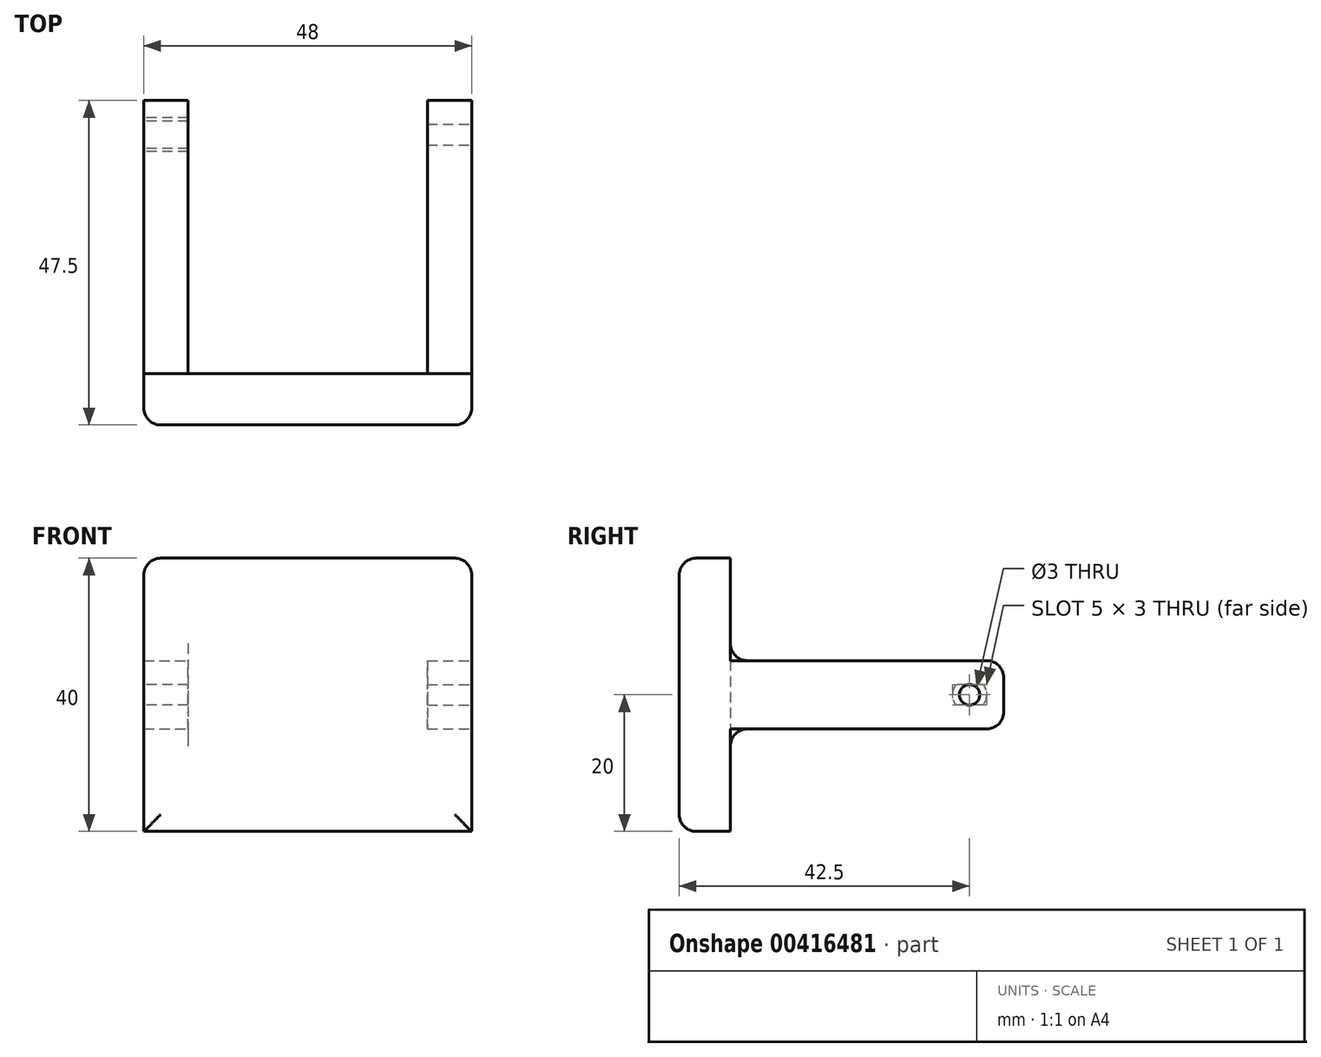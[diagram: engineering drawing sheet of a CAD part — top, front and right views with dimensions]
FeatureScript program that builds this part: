
annotation { "Feature Type Name" : "Feature", "Feature Type Description" : "" }
export const myFeature = defineFeature(function(context is Context, id is Id, definition is map)
    precondition{}
    {
        {
            var Q0;
            Q0=qCreatedBy(makeId("Top.planeOp"),FACE);
            var sketch = newSketch(context, id + "F0", { "sketchPlane" : qUnion([Q0])});
            skLineSegment(sketch, "E0.bottom", {"start": v(-24, 40) * mm, "end": v(24, 40) * mm});
            skLineSegment(sketch, "E0.top", {"start": v(-24, -7.5) * mm, "end": v(24, -7.5) * mm});
            skLineSegment(sketch, "E0.left", {"start": v(-24, 40) * mm, "end": v(-24, -7.5) * mm});
            skLineSegment(sketch, "E0.right", {"start": v(24, 40) * mm, "end": v(24, -7.5) * mm});
            skLineSegment(sketch, "E1.bottom", {"start": v(-17.5, 40) * mm, "end": v(17.5, 40) * mm});
            skLineSegment(sketch, "E1.top", {"start": v(-17.5, 0) * mm, "end": v(17.5, 0) * mm});
            skLineSegment(sketch, "E1.left", {"start": v(-17.5, 40) * mm, "end": v(-17.5, 0) * mm});
            skLineSegment(sketch, "E1.right", {"start": v(17.5, 40) * mm, "end": v(17.5, 0) * mm});
            skPoint(sketch, "E2", {"position": v(0, 40) * mm});
            skPoint(sketch, "E3", {"position": v(0, 0) * mm});
            skLineSegment(sketch, "E4.top", {"start": v(-24, 0) * mm, "end": v(24, 0) * mm});
            skLineSegment(sketch, "E4.left", {"start": v(-24, -7.5) * mm, "end": v(-24, 0) * mm});
            skLineSegment(sketch, "E4.right", {"start": v(24, -7.5) * mm, "end": v(24, 0) * mm});
            skSolve(sketch);
        }
        {
            var Q0;
            {var subQ0=sQuery(id+"F0.wireOp",EDGE,"fILYmVWM-iYGu-gwed-nY9A-4RlSeJw38Jqi.bottom");var subQ1=sQuery(id+"F0.wireOp",EDGE,"E0.left");var subQ2=makeQuery(id+"F0.imprint","INTERSECT",VERTEX,{"derivedFrom":[subQ1,subQ0]});Q0=makeQuery(id+"F0.imprint","IMPRINT",FACE,{"disambiguationData":[TD([[makeQuery(id+"F0.imprint","IMPRINT",EDGE,{"disambiguationData":[TD([[subQ2,1.0]])],"derivedFrom":subQ1}),1.0]])]});}
            var Q1;
            {var subQ3=sQuery(id+"F0.wireOp",EDGE,"E1.left");Q1=makeQuery(id+"F0.imprint","IMPRINT",FACE,{"disambiguationData":[TD([[makeQuery(id+"F0.imprint","IMPRINT",EDGE,{"derivedFrom":subQ3}),-1.0]])]});}
            var Q2;
            {var subQ5=sQuery(id+"F0.wireOp",EDGE,"fILYmVWM-iYGu-gwed-nY9A-4RlSeJw38Jqi.left");Q2=makeQuery(id+"F0.imprint","IMPRINT",FACE,{"disambiguationData":[TD([[makeQuery(id+"F0.imprint","IMPRINT",EDGE,{"derivedFrom":subQ5}),-1.0]])]});}
            var Q3;
            {var subQ3=sQuery(id+"F0.wireOp",EDGE,"E1.right");Q3=makeQuery(id+"F0.imprint","IMPRINT",FACE,{"disambiguationData":[TD([[makeQuery(id+"F0.imprint","IMPRINT",EDGE,{"derivedFrom":subQ3}),1.0]])]});}
            var Q4;
            {var subQ5=sQuery(id+"F0.wireOp",EDGE,"fILYmVWM-iYGu-gwed-nY9A-4RlSeJw38Jqi.right");Q4=makeQuery(id+"F0.imprint","IMPRINT",FACE,{"disambiguationData":[TD([[makeQuery(id+"F0.imprint","IMPRINT",EDGE,{"derivedFrom":subQ5}),1.0]])]});}
            var Q5;
            Q5=makeQuery(id+"F0.imprint","IMPRINT",FACE,{"disambiguationData":[TD([[makeQuery(id+"F0.imprint","IMPRINT",EDGE,{"derivedFrom":sQuery(id+"F0.wireOp",EDGE,"E0.top")}),1.0]])]});
            extrude(context, id + "F1", {"entities" : qUnion([Q0, Q1, Q2, Q3, Q4, Q5]), "depth" : 10 * mm});
        }
        {
            var Q0;
            Q0=makeQuery(id+"F1.opExtrude","SWEPT_FACE",FACE,{"disambiguationData":[OSD([sQuery(id+"F0.wireOp",EDGE,"E0.right")])]});
            var sketch = newSketch(context, id + "F2", { "sketchPlane" : qUnion([Q0])});
            skLineSegment(sketch, "E5", {"start": v(35, 5) * mm, "end": v(40, 5) * mm, "construction": true});
            skCircle(sketch, "E6", {"center": v(35, 5) * mm, "radius": 1.5 * mm});
            skLineSegment(sketch, "E7", {"start": v(0, 0) * mm, "end": v(0, 10) * mm, "construction": true});
            skSolve(sketch);
        }
        {
            var Q0;
            Q0=makeQuery(id+"F1.opExtrude","SWEPT_FACE",FACE,{"disambiguationData":[OSD([sQuery(id+"F0.wireOp",EDGE,"E0.left")])]});
            var sketch = newSketch(context, id + "F3", { "sketchPlane" : qUnion([Q0])});
            skLineSegment(sketch, "E8", {"start": v(-40, 5) * mm, "end": v(-35, 5) * mm, "construction": true});
            skCircle(sketch, "E9", {"center": v(-35, 5) * mm, "radius": 2.5 * mm});
            skLineSegment(sketch, "E10", {"start": v(-37, 6.5) * mm, "end": v(-33, 6.5) * mm});
            skLineSegment(sketch, "E11", {"start": v(-37, 3.5) * mm, "end": v(-33, 3.5) * mm});
            skLineSegment(sketch, "E12", {"start": v(-35, 3.5) * mm, "end": v(-35, 6.5) * mm, "construction": true});
            skLineSegment(sketch, "E13", {"start": v(0, 0) * mm, "end": v(0, 10) * mm, "construction": true});
            skSolve(sketch);
        }
        {
            var Q0;
            {var subQ0=sQuery(id+"F3.wireOp",EDGE,"E10");Q0=makeQuery(id+"F3.imprint","IMPRINT",FACE,{"disambiguationData":[TD([[makeQuery(id+"F3.imprint","IMPRINT",EDGE,{"derivedFrom":subQ0}),-1.0]])]});}
            var Q1;
            Q1=makeQuery(id+"F1.opExtrude","SWEPT_FACE",FACE,{"disambiguationData":[OSD([sQuery(id+"F0.wireOp",EDGE,"E1.left")])]});
            extrude(context, id + "F4", {"entities" : qUnion([Q0]), "operationType" : NewBodyOperationType.REMOVE, "endBound" : BoundingType.UP_TO_SURFACE, "oppositeDirection" : true, "endBoundEntityFace" : qUnion([Q1]), "depth" : 25 * mm});
        }
        {
            var Q0;
            Q0=makeQuery(id+"F2.imprint","IMPRINT",FACE,{"disambiguationData":[TD([[makeQuery(id+"F2.imprint","IMPRINT",EDGE,{"derivedFrom":sQuery(id+"F2.wireOp",EDGE,"E6")}),1.0]])]});
            var Q1;
            Q1=makeQuery(id+"F1.opExtrude","SWEPT_FACE",FACE,{"disambiguationData":[OSD([sQuery(id+"F0.wireOp",EDGE,"E1.right")])]});
            extrude(context, id + "F5", {"entities" : qUnion([Q0]), "operationType" : NewBodyOperationType.REMOVE, "endBound" : BoundingType.UP_TO_SURFACE, "oppositeDirection" : true, "endBoundEntityFace" : qUnion([Q1]), "depth" : 25 * mm});
        }
        {
            var Q0;
            Q0=makeQuery(id+"F1.opExtrude","CAP_FACE",FACE,{"disambiguationData":[OSD([sQuery(id+"F0.wireOp",EDGE,"E0.bottom"),sQuery(id+"F0.wireOp",EDGE,"E0.left"),sQuery(id+"F0.wireOp",EDGE,"E0.right"),sQuery(id+"F0.wireOp",EDGE,"E1.left"),sQuery(id+"F0.wireOp",EDGE,"E1.right"),sQuery(id+"F0.wireOp",EDGE,"E0.top"),sQuery(id+"F0.wireOp",EDGE,"E4.top"),sQuery(id+"F0.wireOp",EDGE,"E4.left"),sQuery(id+"F0.wireOp",EDGE,"E4.right")])],"isStart":false});
            var sketch = newSketch(context, id + "F6", { "sketchPlane" : qUnion([Q0])});
            skLineSegment(sketch, "E14.bottom", {"start": v(-24, 0) * mm, "end": v(24, 0) * mm});
            skLineSegment(sketch, "E14.top", {"start": v(-24, -7.5) * mm, "end": v(24, -7.5) * mm});
            skLineSegment(sketch, "E14.left", {"start": v(-24, 0) * mm, "end": v(-24, -7.5) * mm});
            skLineSegment(sketch, "E14.right", {"start": v(24, 0) * mm, "end": v(24, -7.5) * mm});
            skSolve(sketch);
        }
        {
            var Q0;
            Q0=makeQuery(id+"F6.imprint","IMPRINT",FACE,{"disambiguationData":[TD([[makeQuery(id+"F6.imprint","IMPRINT",EDGE,{"derivedFrom":sQuery(id+"F6.wireOp",EDGE,"E14.top")}),1.0]])]});
            extrude(context, id + "F7", {"entities" : qUnion([Q0]), "operationType" : NewBodyOperationType.ADD, "depth" : 15 * mm});
        }
        {
            var Q0;
            Q0=makeQuery(id+"F0.imprint","IMPRINT",FACE,{"disambiguationData":[TD([[makeQuery(id+"F0.imprint","IMPRINT",EDGE,{"derivedFrom":sQuery(id+"F0.wireOp",EDGE,"E0.top")}),1.0]])]});
            extrude(context, id + "F8", {"entities" : qUnion([Q0]), "operationType" : NewBodyOperationType.ADD, "oppositeDirection" : true, "depth" : 15 * mm});
        }
        {
            var Q0;
            {var subQ0=sQuery(id+"F0.wireOp",EDGE,"E4.left");var subQ1=sQuery(id+"F0.wireOp",EDGE,"E0.top");Q0=makeQuery(id+"F8.boolean.opBoolean","MERGE",EDGE,{"derivedFrom":[makeQuery(id+"F7.boolean.opBoolean","MERGE",EDGE,{"derivedFrom":[makeQuery(id+"F1.opExtrude","SWEPT_EDGE",EDGE,{"disambiguationData":[OSD([subQ1,subQ0])]}),makeQuery(id+"F7.opExtrude","SWEPT_EDGE",EDGE,{"disambiguationData":[OSD([sQuery(id+"F6.wireOp",EDGE,"E14.top"),sQuery(id+"F6.wireOp",EDGE,"E14.left")])]})]}),makeQuery(id+"F8.opExtrude","SWEPT_EDGE",EDGE,{"disambiguationData":[OSD([subQ1,subQ0])]})]});}
            var Q1;
            {var subQ0=sQuery(id+"F0.wireOp",EDGE,"E4.right");var subQ1=sQuery(id+"F0.wireOp",EDGE,"E0.top");Q1=makeQuery(id+"F8.boolean.opBoolean","MERGE",EDGE,{"derivedFrom":[makeQuery(id+"F7.boolean.opBoolean","MERGE",EDGE,{"derivedFrom":[makeQuery(id+"F1.opExtrude","SWEPT_EDGE",EDGE,{"disambiguationData":[OSD([subQ1,subQ0])]}),makeQuery(id+"F7.opExtrude","SWEPT_EDGE",EDGE,{"disambiguationData":[OSD([sQuery(id+"F6.wireOp",EDGE,"E14.top"),sQuery(id+"F6.wireOp",EDGE,"E14.right")])]})]}),makeQuery(id+"F8.opExtrude","SWEPT_EDGE",EDGE,{"disambiguationData":[OSD([subQ1,subQ0])]})]});}
            var Q2;
            {var subQ0=sQuery(id+"F0.wireOp",EDGE,"E0.bottom");Q2=makeQuery(id+"F1.opExtrude","CAP_EDGE",EDGE,{"disambiguationData":[OSD([subQ0]),TDD([makeQuery(id+"F0.imprint","IMPRINT",EDGE,{"disambiguationData":[TD([[makeQuery(id+"F0.imprint","INTERSECT",VERTEX,{"derivedFrom":[subQ0,sQuery(id+"F0.wireOp",EDGE,"E0.left")]}),-1.0]])],"derivedFrom":subQ0})])],"isStart":false});}
            var Q3;
            {var subQ0=sQuery(id+"F0.wireOp",EDGE,"E0.bottom");Q3=makeQuery(id+"F1.opExtrude","CAP_EDGE",EDGE,{"disambiguationData":[OSD([subQ0]),TDD([makeQuery(id+"F0.imprint","IMPRINT",EDGE,{"disambiguationData":[TD([[makeQuery(id+"F0.imprint","INTERSECT",VERTEX,{"derivedFrom":[subQ0,sQuery(id+"F0.wireOp",EDGE,"E0.left")]}),-1.0]])],"derivedFrom":subQ0})])],"isStart":true});}
            var Q4;
            {var subQ0=sQuery(id+"F0.wireOp",EDGE,"E0.bottom");Q4=makeQuery(id+"F1.opExtrude","CAP_EDGE",EDGE,{"disambiguationData":[OSD([subQ0]),TDD([makeQuery(id+"F0.imprint","IMPRINT",EDGE,{"disambiguationData":[TD([[makeQuery(id+"F0.imprint","INTERSECT",VERTEX,{"derivedFrom":[subQ0,sQuery(id+"F0.wireOp",EDGE,"E0.right")]}),1.0]])],"derivedFrom":subQ0})])],"isStart":false});}
            var Q5;
            {var subQ0=sQuery(id+"F0.wireOp",EDGE,"E0.bottom");Q5=makeQuery(id+"F1.opExtrude","CAP_EDGE",EDGE,{"disambiguationData":[OSD([subQ0]),TDD([makeQuery(id+"F0.imprint","IMPRINT",EDGE,{"disambiguationData":[TD([[makeQuery(id+"F0.imprint","INTERSECT",VERTEX,{"derivedFrom":[subQ0,sQuery(id+"F0.wireOp",EDGE,"E0.right")]}),1.0]])],"derivedFrom":subQ0})])],"isStart":true});}
            var Q6;
            Q6=makeQuery(id+"F7.opExtrude","CAP_EDGE",EDGE,{"disambiguationData":[OSD([sQuery(id+"F6.wireOp",EDGE,"E14.top")])],"isStart":false});
            var Q7;
            Q7=makeQuery(id+"F7.opExtrude","CAP_EDGE",EDGE,{"disambiguationData":[OSD([sQuery(id+"F6.wireOp",EDGE,"E14.right")])],"isStart":false});
            var Q8;
            Q8=makeQuery(id+"F7.opExtrude","CAP_EDGE",EDGE,{"disambiguationData":[OSD([sQuery(id+"F6.wireOp",EDGE,"E14.left")])],"isStart":false});
            var Q9;
            Q9=makeQuery(id+"F8.opExtrude","CAP_EDGE",EDGE,{"disambiguationData":[OSD([sQuery(id+"F0.wireOp",EDGE,"E4.left")])],"isStart":false});
            var Q10;
            Q10=makeQuery(id+"F8.opExtrude","CAP_EDGE",EDGE,{"disambiguationData":[OSD([sQuery(id+"F0.wireOp",EDGE,"E4.right")])],"isStart":false});
            var Q11;
            Q11=makeQuery(id+"F8.opExtrude","CAP_EDGE",EDGE,{"disambiguationData":[OSD([sQuery(id+"F0.wireOp",EDGE,"E0.top")])],"isStart":false});
            var Q12;
            {var subQ3=sQuery(id+"F0.wireOp",EDGE,"E1.right");var subQ4=sQuery(id+"F6.wireOp",EDGE,"E14.bottom");Q12=makeQuery(id+"F7.boolean.opBoolean","SPLIT",EDGE,{"disambiguationData":[TD([makeQuery(id+"F1.opExtrude","SWEPT_FACE",FACE,{"disambiguationData":[OSD([subQ3])]})])],"derivedFrom":makeQuery(id+"F7.opExtrude","CAP_EDGE",EDGE,{"disambiguationData":[OSD([subQ4])],"isStart":true})});}
            var Q13;
            {var subQ0=sQuery(id+"F0.wireOp",EDGE,"E4.top");var subQ1=sQuery(id+"F0.wireOp",EDGE,"E1.right");Q13=makeQuery(id+"F8.boolean.opBoolean","SPLIT",EDGE,{"disambiguationData":[TD([makeQuery(id+"F1.opExtrude","SWEPT_FACE",FACE,{"disambiguationData":[OSD([subQ1])]})])],"derivedFrom":makeQuery(id+"F8.opExtrude","CAP_EDGE",EDGE,{"disambiguationData":[OSD([subQ0])],"isStart":true})});}
            var Q14;
            {var subQ0=sQuery(id+"F0.wireOp",EDGE,"E1.left");var subQ4=sQuery(id+"F6.wireOp",EDGE,"E14.bottom");Q14=makeQuery(id+"F7.boolean.opBoolean","SPLIT",EDGE,{"disambiguationData":[TD([makeQuery(id+"F1.opExtrude","SWEPT_FACE",FACE,{"disambiguationData":[OSD([subQ0])]})])],"derivedFrom":makeQuery(id+"F7.opExtrude","CAP_EDGE",EDGE,{"disambiguationData":[OSD([subQ4])],"isStart":true})});}
            var Q15;
            {var subQ0=sQuery(id+"F0.wireOp",EDGE,"E4.top");var subQ3=sQuery(id+"F0.wireOp",EDGE,"E1.left");Q15=makeQuery(id+"F8.boolean.opBoolean","SPLIT",EDGE,{"disambiguationData":[TD([makeQuery(id+"F1.opExtrude","SWEPT_FACE",FACE,{"disambiguationData":[OSD([subQ3])]})])],"derivedFrom":makeQuery(id+"F8.opExtrude","CAP_EDGE",EDGE,{"disambiguationData":[OSD([subQ0])],"isStart":true})});}
            fillet(context, id + "F9", {"entities" : qUnion([Q0, Q1, Q2, Q3, Q4, Q5, Q6, Q7, Q8, Q9, Q10, Q11, Q12, Q13, Q14, Q15]), "radius" : 2.5 * mm, "tangentPropagation" : true, "allowEdgeOverflow" : false});
        }
    });
